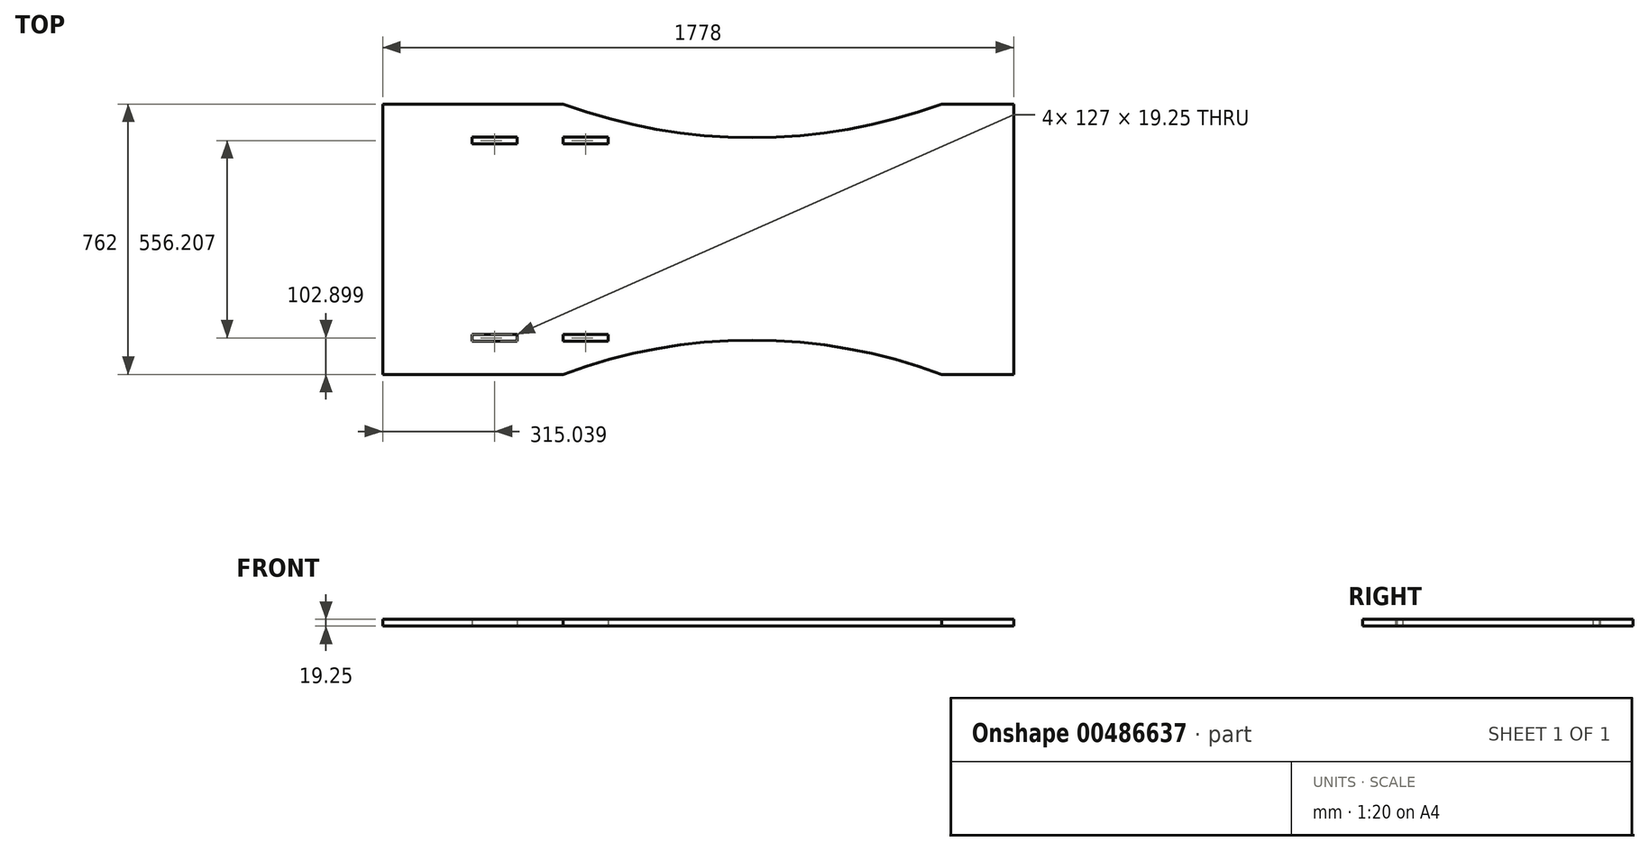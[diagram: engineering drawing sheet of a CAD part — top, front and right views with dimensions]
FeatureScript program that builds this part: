
annotation { "Feature Type Name" : "Feature", "Feature Type Description" : "" }
export const myFeature = defineFeature(function(context is Context, id is Id, definition is map)
    precondition{}
    {
        {
            var Q0;
            Q0=qCreatedBy(makeId("Top.planeOp"),FACE);
            var sketch = newSketch(context, id + "F0", { "sketchPlane" : qUnion([Q0])});
            skLineSegment(sketch, "E0.bottom", {"start": v(-121.81, 705.75) * mm, "end": v(259.19, 705.75) * mm});
            skLineSegment(sketch, "E0.top", {"start": v(-121.81, -56.25) * mm, "end": v(259.19, -56.25) * mm});
            skLineSegment(sketch, "E0.left", {"start": v(-121.81, 705.75) * mm, "end": v(-121.81, -56.25) * mm});
            skLineSegment(sketch, "E0.right", {"start": v(1656.19, 705.75) * mm, "end": v(1656.19, -56.25) * mm});
            skLineSegment(sketch, "E1.trimOffspring", {"start": v(1452.99, 705.75) * mm, "end": v(1656.19, 705.75) * mm});
            skLineSegment(sketch, "E2.trimOffspring", {"start": v(1452.99, -56.25) * mm, "end": v(1656.19, -56.25) * mm});
            skLineSegment(sketch, "E3", {"start": v(259.19, 705.75) * mm, "end": v(386.19, 705.75) * mm});
            skLineSegment(sketch, "E4", {"start": v(259.19, -56.25) * mm, "end": v(386.19, -56.25) * mm});
            skArc(sketch, "E5", {"start": v(386.19, 705.75) * mm, "mid": v(919.59, 610.93) * mm, "end": v(1452.99, 705.75) * mm});
            skArc(sketch, "E6", {"start": v(1452.99, -56.25) * mm, "mid": v(919.59, 40.15) * mm, "end": v(386.19, -56.25) * mm});
            skPoint(sketch, "E7.orphan", {"position": v(911.43, 705.75) * mm});
            skPoint(sketch, "E8.orphan", {"position": v(911.43, -56.25) * mm});
            skLineSegment(sketch, "E9", {"start": v(-121.81, 687.48) * mm, "end": v(18.9, 687.48) * mm, "construction": true});
            skLineSegment(sketch, "E10", {"start": v(18.9, 687.48) * mm, "end": v(18.9, 705.75) * mm, "construction": true});
            skLineSegment(sketch, "E11", {"start": v(386.19, 705.75) * mm, "end": v(-121.81, 705.75) * mm, "construction": true});
            skLineSegment(sketch, "E12", {"start": v(386.19, 37.02) * mm, "end": v(386.19, 56.28) * mm});
            skLineSegment(sketch, "E13", {"start": v(386.19, 56.28) * mm, "end": v(513.19, 56.28) * mm});
            skLineSegment(sketch, "E14", {"start": v(513.19, 56.28) * mm, "end": v(513.19, 37.02) * mm});
            skLineSegment(sketch, "E15", {"start": v(513.19, 37.02) * mm, "end": v(386.19, 37.02) * mm});
            skLineSegment(sketch, "E16", {"start": v(386.19, 612.48) * mm, "end": v(513.19, 612.48) * mm});
            skLineSegment(sketch, "E17", {"start": v(513.19, 612.48) * mm, "end": v(513.19, 593.23) * mm});
            skLineSegment(sketch, "E18", {"start": v(513.19, 593.23) * mm, "end": v(386.19, 593.23) * mm});
            skLineSegment(sketch, "E19", {"start": v(386.19, 593.23) * mm, "end": v(386.19, 612.48) * mm});
            skLineSegment(sketch, "E20", {"start": v(256.73, 612.48) * mm, "end": v(256.73, 593.23) * mm});
            skLineSegment(sketch, "E21", {"start": v(256.73, 593.23) * mm, "end": v(129.73, 593.23) * mm});
            skLineSegment(sketch, "E22", {"start": v(129.73, 593.23) * mm, "end": v(129.73, 612.48) * mm});
            skLineSegment(sketch, "E23", {"start": v(129.73, 612.48) * mm, "end": v(256.73, 612.48) * mm});
            skLineSegment(sketch, "E24", {"start": v(256.73, 56.28) * mm, "end": v(129.73, 56.28) * mm});
            skLineSegment(sketch, "E25", {"start": v(129.73, 56.28) * mm, "end": v(129.73, 37.02) * mm});
            skLineSegment(sketch, "E26", {"start": v(129.73, 37.02) * mm, "end": v(256.73, 37.02) * mm});
            skLineSegment(sketch, "E27", {"start": v(256.73, 37.02) * mm, "end": v(256.73, 56.28) * mm});
            skSolve(sketch);
        }
        {
            var Q0;
            Q0=makeQuery(id+"F0.imprint","IMPRINT",FACE,{"disambiguationData":[TD([[makeQuery(id+"F0.imprint","IMPRINT",EDGE,{"derivedFrom":sQuery(id+"F0.wireOp",EDGE,"E0.bottom")}),-1.0]])]});
            extrude(context, id + "F1", {"entities" : qUnion([Q0]), "depth" : 19.25 * mm, "offsetDistance" : 25.4 * mm});
        }
    });
